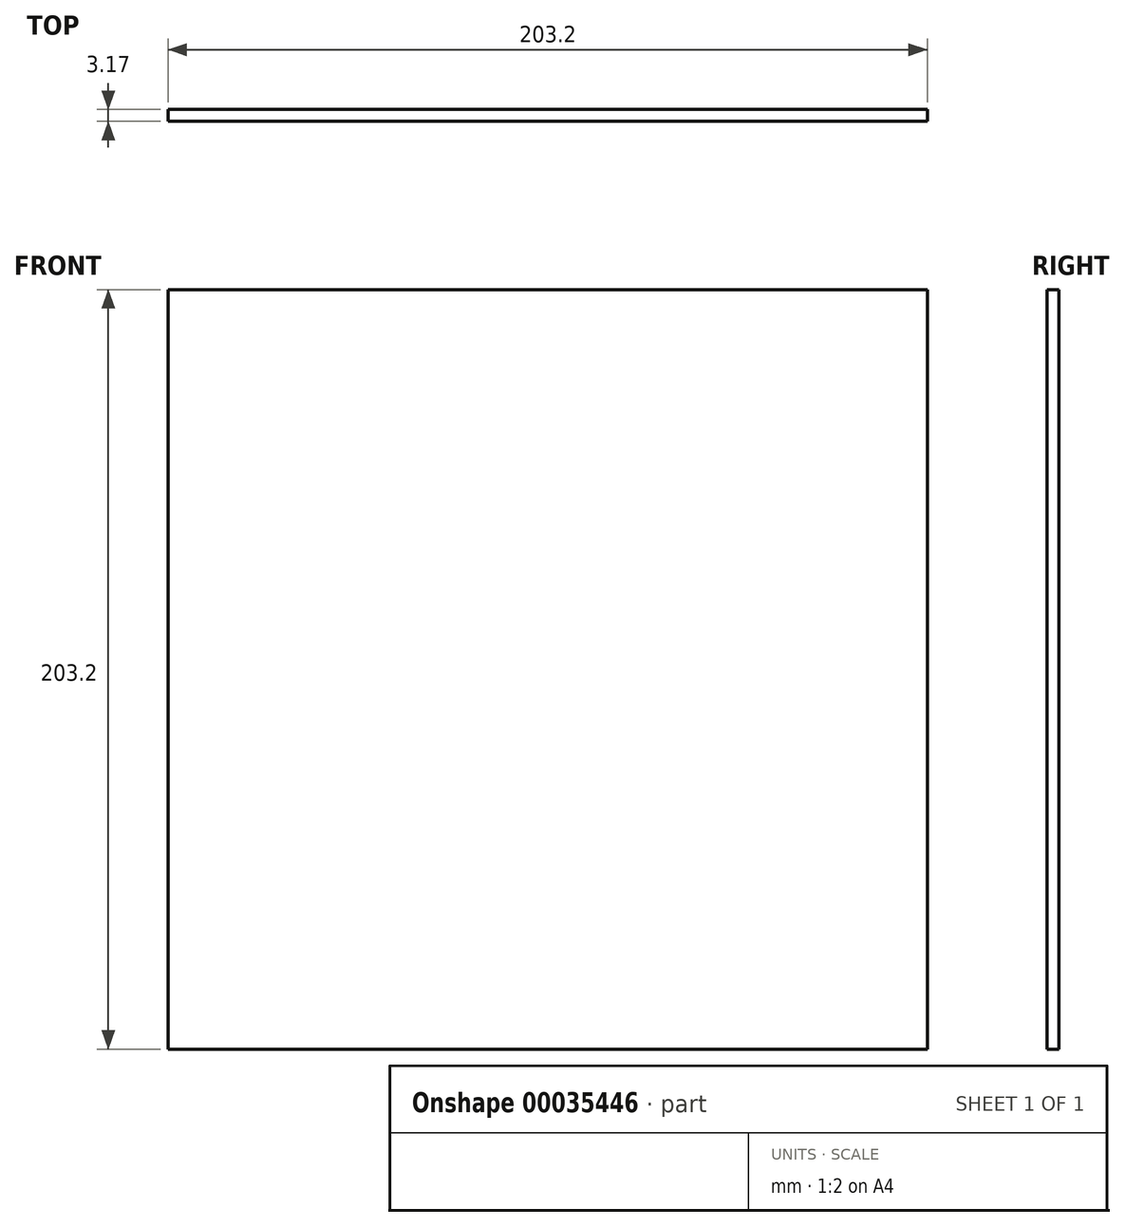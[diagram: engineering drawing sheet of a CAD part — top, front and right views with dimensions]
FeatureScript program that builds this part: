
annotation { "Feature Type Name" : "Feature", "Feature Type Description" : "" }
export const myFeature = defineFeature(function(context is Context, id is Id, definition is map)
    precondition{}
    {
        {
            var Q0;
            Q0=qCreatedBy(makeId("Front.planeOp"),FACE);
            var sketch = newSketch(context, id + "F0", { "sketchPlane" : qUnion([Q0])});
            skLineSegment(sketch, "E0.bottom", {"start": v(-105.22, 96.23) * mm, "end": v(-54.42, 96.23) * mm});
            skLineSegment(sketch, "E0.top", {"start": v(-105.22, -106.97) * mm, "end": v(-54.42, -106.97) * mm});
            skLineSegment(sketch, "E0.left", {"start": v(-105.22, 96.23) * mm, "end": v(-105.22, -106.97) * mm});
            skLineSegment(sketch, "E0.right", {"start": v(-54.42, 96.23) * mm, "end": v(-54.42, -106.97) * mm});
            skLineSegment(sketch, "E1.bottom", {"start": v(-54.42, 96.23) * mm, "end": v(-3.62, 96.23) * mm});
            skLineSegment(sketch, "E1.top", {"start": v(-54.42, -106.97) * mm, "end": v(-3.62, -106.97) * mm});
            skLineSegment(sketch, "E1.right", {"start": v(-3.62, 96.23) * mm, "end": v(-3.62, -106.97) * mm});
            skLineSegment(sketch, "E2.bottom", {"start": v(-3.62, 96.23) * mm, "end": v(47.18, 96.23) * mm});
            skLineSegment(sketch, "E2.top", {"start": v(-3.62, -106.97) * mm, "end": v(47.18, -106.97) * mm});
            skLineSegment(sketch, "E2.right", {"start": v(47.18, 96.23) * mm, "end": v(47.18, -106.97) * mm});
            skLineSegment(sketch, "E3.bottom", {"start": v(47.18, 96.23) * mm, "end": v(97.98, 96.23) * mm});
            skLineSegment(sketch, "E3.top", {"start": v(47.18, -106.97) * mm, "end": v(97.98, -106.97) * mm});
            skLineSegment(sketch, "E3.right", {"start": v(97.98, 96.23) * mm, "end": v(97.98, -106.97) * mm});
            skSolve(sketch);
        }
        {
            var Q0;
            Q0 = qSketchRegion(id + "F0", true);
            extrude(context, id + "F1", {"entities" : qUnion([Q0]), "depth" : 3.17 * mm});
        }
    });
